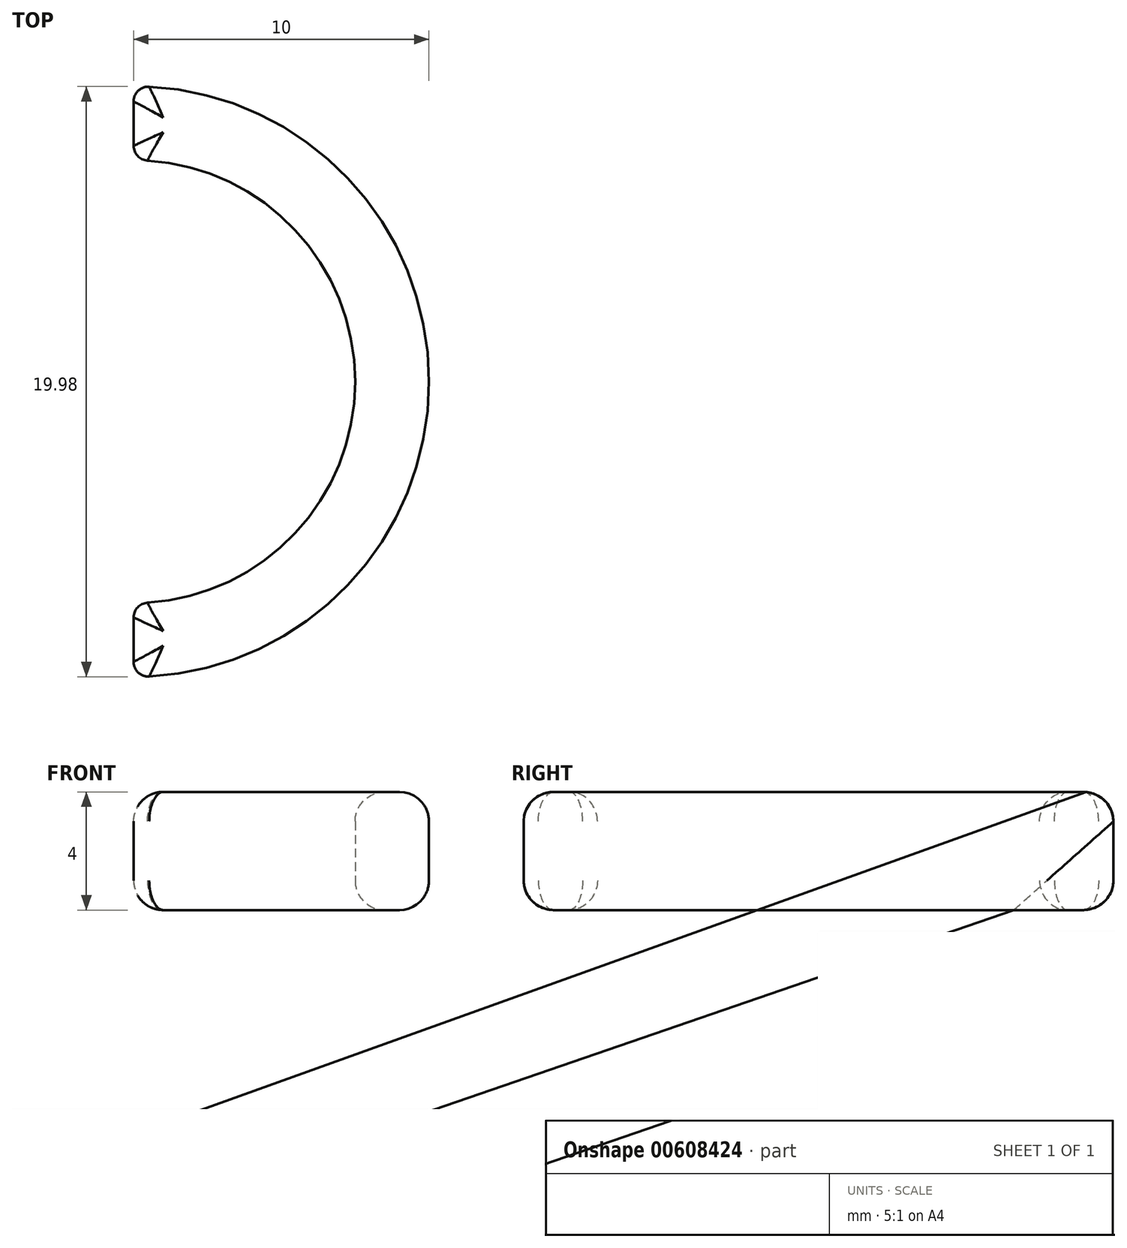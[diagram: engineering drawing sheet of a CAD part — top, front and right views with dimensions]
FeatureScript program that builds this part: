
annotation { "Feature Type Name" : "Feature", "Feature Type Description" : "" }
export const myFeature = defineFeature(function(context is Context, id is Id, definition is map)
    precondition{}
    {
        {
            var Q0;
            Q0=qCreatedBy(makeId("Top.planeOp"),FACE);
            var sketch = newSketch(context, id + "F0", { "sketchPlane" : qUnion([Q0])});
            skLineSegment(sketch, "E0", {"start": v(0, 0) * mm, "end": v(0, 7.5) * mm, "construction": true});
            skLineSegment(sketch, "E1", {"start": v(0, 0) * mm, "end": v(-5.03, -5.57) * mm, "construction": true});
            skPoint(sketch, "E2", {"position": v(-5.03, -5.57) * mm});
            skPoint(sketch, "E3", {"position": v(0, 7.5) * mm});
            skPoint(sketch, "E4", {"position": v(0, 10) * mm});
            skArc(sketch, "E5", {"start": v(0, 10) * mm, "mid": v(-9.33, 3.6) * mm, "end": v(-6.7, -7.42) * mm, "construction": true});
            skLineSegment(sketch, "E6", {"start": v(0, 7.5) * mm, "end": v(0, 7.5) * mm});
            skLineSegment(sketch, "E7", {"start": v(-5.03, -5.57) * mm, "end": v(-5.03, -5.57) * mm});
            skArc(sketch, "E8", {"start": v(0, 7.5) * mm, "mid": v(-7, 2.7) * mm, "end": v(-5.03, -5.57) * mm, "construction": true});
            skLineSegment(sketch, "E9", {"start": v(0, 7.5) * mm, "end": v(0, 10) * mm});
            skLineSegment(sketch, "E10", {"start": v(0, 0) * mm, "end": v(0, -7.5) * mm, "construction": true});
            skArc(sketch, "E11", {"start": v(0, -7.5) * mm, "mid": v(7.5, 0) * mm, "end": v(0, 7.5) * mm});
            skArc(sketch, "E12", {"start": v(0, -10) * mm, "mid": v(10, 0) * mm, "end": v(0, 10) * mm});
            skLineSegment(sketch, "E13", {"start": v(0, -7.5) * mm, "end": v(0, -10) * mm});
            skSolve(sketch);
        }
        {
            var Q0;
            Q0 = qSketchRegion(id + "F0", true);
            extrude(context, id + "F1", {"entities" : qUnion([Q0]), "depth" : 4 * mm, "offsetDistance" : 25 * mm});
        }
        {
            var Q0;
            Q0=makeQuery(id+"F1.opExtrude","CAP_FACE",FACE,{"disambiguationData":[OSD([sQuery(id+"F0.wireOp",EDGE,"E9"),sQuery(id+"F0.wireOp",EDGE,"E11"),sQuery(id+"F0.wireOp",EDGE,"E12"),sQuery(id+"F0.wireOp",EDGE,"E13")])],"isStart":true});
            var Q1;
            Q1=makeQuery(id+"F1.opExtrude","CAP_FACE",FACE,{"disambiguationData":[OSD([sQuery(id+"F0.wireOp",EDGE,"E9"),sQuery(id+"F0.wireOp",EDGE,"E11"),sQuery(id+"F0.wireOp",EDGE,"E12"),sQuery(id+"F0.wireOp",EDGE,"E13")])],"isStart":false});
            fillet(context, id + "F2", {"entities" : qUnion([Q0, Q1]), "radius" : 1 * mm, "tangentPropagation" : true, "allowEdgeOverflow" : false});
        }
        {
            var Q0;
            Q0=makeQuery(id+"F2.opFillet","BLEND_FACE",FACE,{"disambiguationData":[OSD([sQuery(id+"F0.wireOp",EDGE,"E9")])]});
            var Q1;
            Q1=makeQuery(id+"F2.opFillet","BLEND_FACE",FACE,{"disambiguationData":[OSD([sQuery(id+"F0.wireOp",EDGE,"E13")])]});
            fillet(context, id + "F3", {"entities" : qUnion([Q0, Q1]), "radius" : 0.5 * mm, "tangentPropagation" : true, "allowEdgeOverflow" : false});
        }
    });
